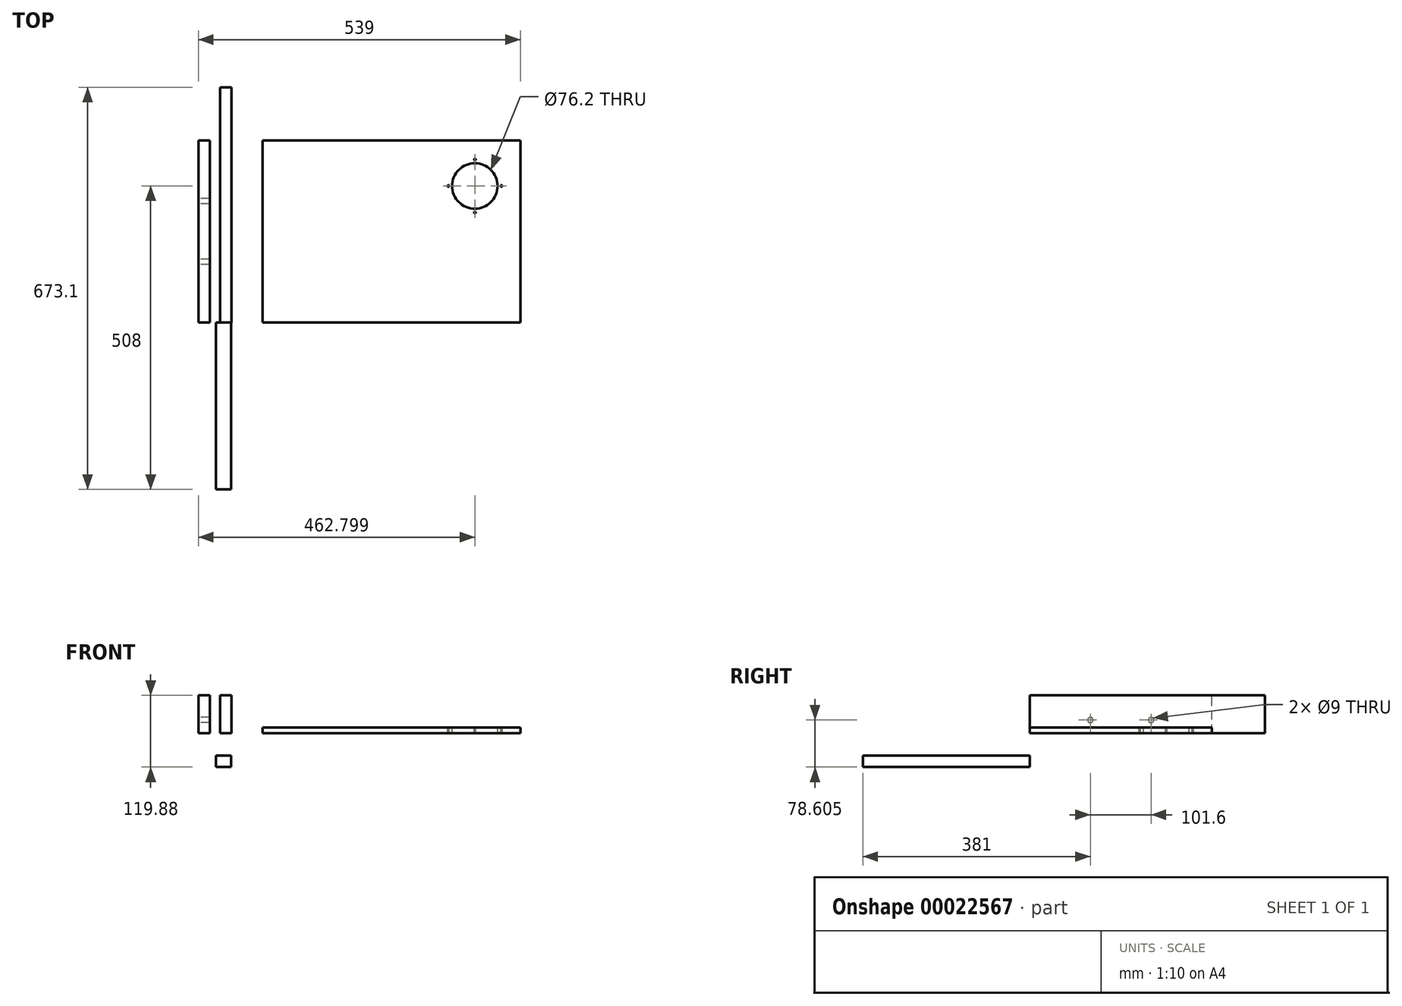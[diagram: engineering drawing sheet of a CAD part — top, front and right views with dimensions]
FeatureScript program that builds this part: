
annotation { "Feature Type Name" : "Feature", "Feature Type Description" : "" }
export const myFeature = defineFeature(function(context is Context, id is Id, definition is map)
    precondition{}
    {
        {
            var Q0;
            Q0=qCreatedBy(makeId("Front.planeOp"),FACE);
            var sketch = newSketch(context, id + "F0", { "sketchPlane" : qUnion([Q0])});
            skLineSegment(sketch, "E0.bottom", {"start": v(0, 0) * mm, "end": v(19.05, 0) * mm});
            skLineSegment(sketch, "E0.top", {"start": v(0, 63.5) * mm, "end": v(19.05, 63.5) * mm});
            skLineSegment(sketch, "E0.left", {"start": v(0, 0) * mm, "end": v(0, 63.5) * mm});
            skLineSegment(sketch, "E0.right", {"start": v(19.05, 0) * mm, "end": v(19.05, 63.5) * mm});
            skSolve(sketch);
        }
        {
            var Q0;
            Q0=qSketchRegion(id+"F0",true);
            extrude(context, id + "F1", {"entities" : qUnion([Q0]), "oppositeDirection" : true, "depth" : 304.8 * mm});
        }
        {
            var Q0;
            Q0=qCreatedBy(makeId("Front.planeOp"),FACE);
            var sketch = newSketch(context, id + "F2", { "sketchPlane" : qUnion([Q0])});
            skLineSegment(sketch, "E1.bottom", {"start": v(36, 0) * mm, "end": v(55.05, 0) * mm});
            skLineSegment(sketch, "E1.top", {"start": v(36, 63.5) * mm, "end": v(55.05, 63.5) * mm});
            skLineSegment(sketch, "E1.left", {"start": v(36, 0) * mm, "end": v(36, 63.5) * mm});
            skLineSegment(sketch, "E1.right", {"start": v(55.05, 0) * mm, "end": v(55.05, 63.5) * mm});
            skSolve(sketch);
        }
        {
            var Q0;
            Q0=qSketchRegion(id+"F2",true);
            extrude(context, id + "F3", {"entities" : qUnion([Q0]), "oppositeDirection" : true, "depth" : 393.7 * mm});
        }
        {
            var Q0;
            Q0=qCreatedBy(makeId("Front.planeOp"),FACE);
            var sketch = newSketch(context, id + "F4", { "sketchPlane" : qUnion([Q0])});
            skLineSegment(sketch, "E2.bottom", {"start": v(107.2, 0) * mm, "end": v(539, 0) * mm});
            skLineSegment(sketch, "E2.top", {"start": v(107.2, 9.52) * mm, "end": v(539, 9.52) * mm});
            skLineSegment(sketch, "E2.left", {"start": v(107.2, 0) * mm, "end": v(107.2, 9.52) * mm});
            skLineSegment(sketch, "E2.right", {"start": v(539, 0) * mm, "end": v(539, 9.52) * mm});
            skSolve(sketch);
        }
        {
            var Q0;
            Q0=qSketchRegion(id+"F4",true);
            extrude(context, id + "F5", {"entities" : qUnion([Q0]), "oppositeDirection" : true, "depth" : 304.8 * mm});
        }
        {
            var Q0;
            Q0=makeQuery(id+"F1.opExtrude","SWEPT_FACE",FACE,{"disambiguationData":[OSD([sQuery(id+"F0.wireOp",EDGE,"E0.left")])]});
            var sketch = newSketch(context, id + "F6", { "sketchPlane" : qUnion([Q0])});
            skLineSegment(sketch, "E3", {"start": v(-304.8, 22.23) * mm, "end": v(0, 22.23) * mm, "construction": true});
            skCircle(sketch, "E4", {"center": v(-203.2, 22.23) * mm, "radius": 4.5 * mm});
            skCircle(sketch, "E5", {"center": v(-101.6, 22.23) * mm, "radius": 4.5 * mm});
            skSolve(sketch);
        }
        {
            var Q0;
            Q0=qSketchRegion(id+"F6",true);
            extrude(context, id + "F7", {"entities" : qUnion([Q0]), "operationType" : NewBodyOperationType.REMOVE, "endBound" : BoundingType.UP_TO_NEXT, "oppositeDirection" : true, "depth" : 25.4 * mm});
        }
        {
            var Q0;
            Q0=qCreatedBy(makeId("Front.planeOp"),FACE);
            var sketch = newSketch(context, id + "F8", { "sketchPlane" : qUnion([Q0])});
            skLineSegment(sketch, "E6.bottom", {"start": v(29.35, -37.33) * mm, "end": v(54.75, -37.33) * mm});
            skLineSegment(sketch, "E6.top", {"start": v(29.35, -56.38) * mm, "end": v(54.75, -56.38) * mm});
            skLineSegment(sketch, "E6.left", {"start": v(29.35, -37.33) * mm, "end": v(29.35, -56.38) * mm});
            skLineSegment(sketch, "E6.right", {"start": v(54.75, -37.33) * mm, "end": v(54.75, -56.38) * mm});
            skSolve(sketch);
        }
        {
            var Q0;
            Q0=qSketchRegion(id+"F8",true);
            extrude(context, id + "F9", {"entities" : qUnion([Q0]), "depth" : 279.4 * mm});
        }
        {
            var Q0;
            Q0=makeQuery(id+"F5.opExtrude","SWEPT_FACE",FACE,{"disambiguationData":[OSD([sQuery(id+"F4.wireOp",EDGE,"E2.top")])]});
            var sketch = newSketch(context, id + "F10", { "sketchPlane" : qUnion([Q0])});
            skCircle(sketch, "E7", {"center": v(462.8, 228.6) * mm, "radius": 38.1 * mm});
            skLineSegment(sketch, "E8", {"start": v(418.35, 228.6) * mm, "end": v(507.25, 228.6) * mm, "construction": true});
            skLineSegment(sketch, "E9", {"start": v(462.8, 273.05) * mm, "end": v(462.8, 184.15) * mm, "construction": true});
            skPoint(sketch, "E10", {"position": v(507.25, 228.6) * mm});
            skPoint(sketch, "E11", {"position": v(462.8, 273.05) * mm});
            skPoint(sketch, "E12", {"position": v(418.35, 228.6) * mm});
            skPoint(sketch, "E13", {"position": v(462.8, 184.15) * mm});
            skSolve(sketch);
        }
        {
            var Q0;
            Q0 = qSketchRegion(id + "F10", true);
            extrude(context, id + "F11", {"entities" : qUnion([Q0]), "operationType" : NewBodyOperationType.REMOVE, "endBound" : BoundingType.UP_TO_NEXT, "oppositeDirection" : true, "depth" : 25.4 * mm});
        }
        {
            var Q0;
            Q0=sQuery(id+"F10.wireOp",VERTEX,"E11");
            var Q1;
            Q1=sQuery(id+"F10.wireOp",VERTEX,"E10");
            var Q2;
            Q2=sQuery(id+"F10.wireOp",VERTEX,"E13");
            var Q3;
            Q3=sQuery(id+"F10.wireOp",VERTEX,"E12");
            var Q4;
            Q4=makeQuery(id+"F5.opExtrude","SWEPT_BODY",BODY,{"disambiguationData":[OSD([sQuery(id+"F4.wireOp",EDGE,"E2.bottom"),sQuery(id+"F4.wireOp",EDGE,"E2.top"),sQuery(id+"F4.wireOp",EDGE,"E2.left"),sQuery(id+"F4.wireOp",EDGE,"E2.right")])]});
            hole(context, id + "F12", {"style" : HoleStyle.SIMPLE, "holeDiameter" : 2.72 * mm, "endStyle" : HoleEndStyle.THROUGH, "locations" : qUnion([Q0, Q1, Q2, Q3]), "scope" : qUnion([Q4])});
        }
    });
